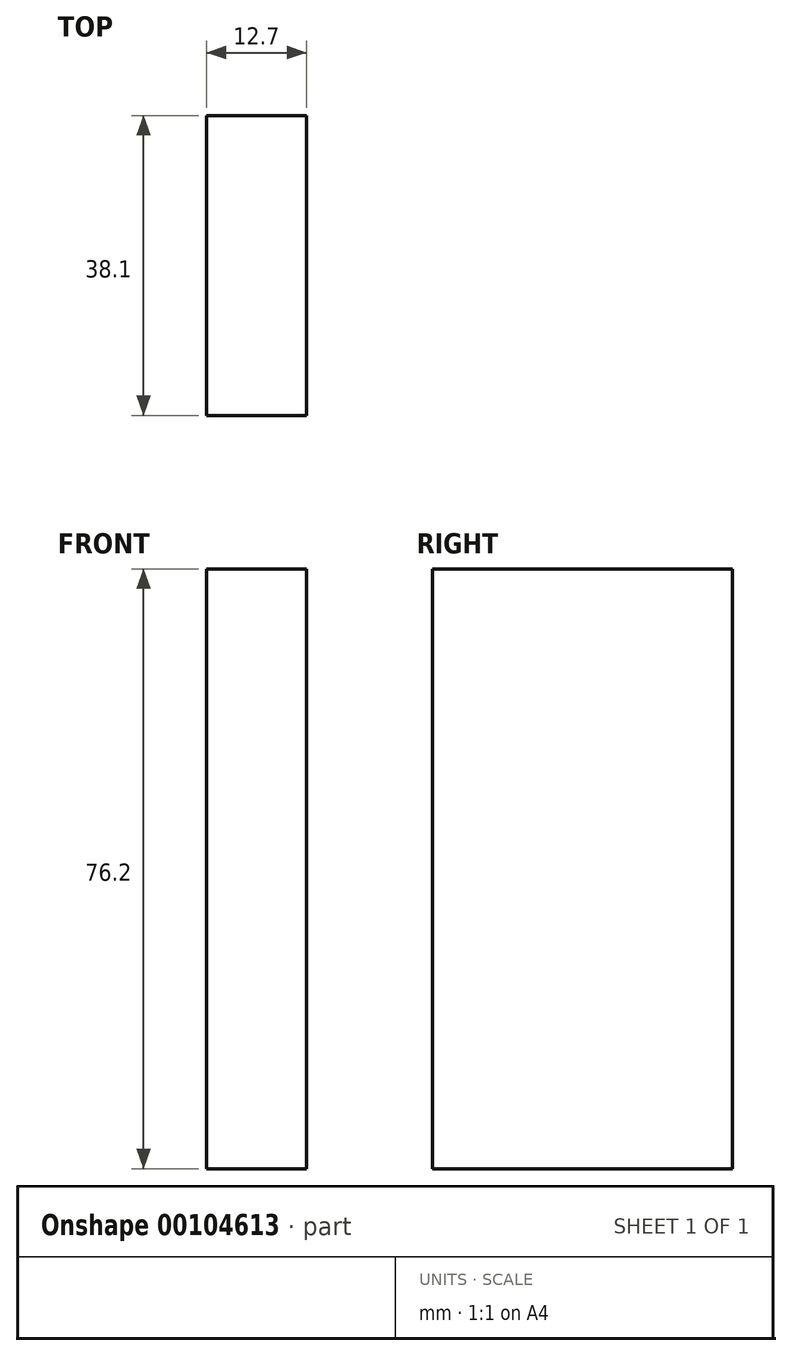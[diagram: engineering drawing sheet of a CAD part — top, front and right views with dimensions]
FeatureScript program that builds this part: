
annotation { "Feature Type Name" : "Feature", "Feature Type Description" : "" }
export const myFeature = defineFeature(function(context is Context, id is Id, definition is map)
    precondition{}
    {
        {
            var Q0;
            Q0=qCreatedBy(makeId("Right.planeOp"),FACE);
            var sketch = newSketch(context, id + "F0", { "sketchPlane" : qUnion([Q0])});
            skLineSegment(sketch, "E0.bottom", {"start": v(-18.75, 66.7) * mm, "end": v(19.35, 66.7) * mm});
            skLineSegment(sketch, "E0.top", {"start": v(-18.75, -9.5) * mm, "end": v(19.35, -9.5) * mm});
            skLineSegment(sketch, "E0.left", {"start": v(-18.75, 66.7) * mm, "end": v(-18.75, -9.5) * mm});
            skLineSegment(sketch, "E0.right", {"start": v(19.35, 66.7) * mm, "end": v(19.35, -9.5) * mm});
            skLineSegment(sketch, "E1.bottom", {"start": v(19.35, 66.7) * mm, "end": v(-18.75, 66.7) * mm});
            skLineSegment(sketch, "E1.top", {"start": v(19.35, 28.6) * mm, "end": v(-18.75, 28.6) * mm});
            skLineSegment(sketch, "E1.left", {"start": v(19.35, 66.7) * mm, "end": v(19.35, 28.6) * mm});
            skLineSegment(sketch, "E1.right", {"start": v(-18.75, 66.7) * mm, "end": v(-18.75, 28.6) * mm});
            skSolve(sketch);
        }
        {
            var Q0;
            Q0 = qSketchRegion(id + "F0", true);
            extrude(context, id + "F1", {"entities" : qUnion([Q0]), "depth" : 12.7 * mm});
        }
        {
            var Q0;
            Q0=makeQuery(id+"F1.opExtrude","CAP_FACE",FACE,{"disambiguationData":[OSD([sQuery(id+"F0.wireOp",EDGE,"E0.top"),sQuery(id+"F0.wireOp",EDGE,"E0.left"),sQuery(id+"F0.wireOp",EDGE,"E0.right"),sQuery(id+"F0.wireOp",EDGE,"E1.bottom"),sQuery(id+"F0.wireOp",EDGE,"E1.left"),sQuery(id+"F0.wireOp",EDGE,"E1.right")])],"isStart":false});
            var sketch = newSketch(context, id + "F2", { "sketchPlane" : qUnion([Q0])});
            skLineSegment(sketch, "E2.bottom", {"start": v(-18.75, 66.7) * mm, "end": v(19.35, 66.7) * mm});
            skLineSegment(sketch, "E2.top", {"start": v(-18.75, 28.6) * mm, "end": v(19.35, 28.6) * mm});
            skLineSegment(sketch, "E2.left", {"start": v(-18.75, 66.7) * mm, "end": v(-18.75, 28.6) * mm});
            skLineSegment(sketch, "E2.right", {"start": v(19.35, 66.7) * mm, "end": v(19.35, 28.6) * mm});
            skSolve(sketch);
        }
    });
